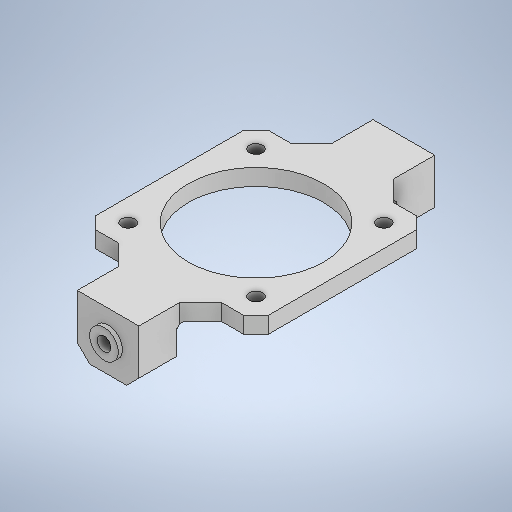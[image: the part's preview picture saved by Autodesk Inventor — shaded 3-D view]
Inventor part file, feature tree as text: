
AUTODESK INVENTOR PART (.ipt)
format: ipt  version: 2025 (Build 290162010, 162A)  size: 352,768 bytes
history: native  units: in
note: dims shown in document units (in); Inventor stores cm internally (conversion verified against a paired STEP export)
features: extrude x5, sketch x5, chamfer x3
ambient origin geometry x8: Origin, YZ Plane, XZ Plane, XY Plane, X Axis, Y Axis, Z Axis, Center Point
bodies: Body1 (feature_tree)
feature tree (13):
  extrude  "Extrusion24"  Depth=1.6535in
  extrude  "Extrusion25"  Depth=1.2248in
  extrude  "Extrusion26"  Depth=0.5906in
  chamfer  "Fasen5"  Distance=0.3642in
  chamfer  "Fasen6"  Distance=0.3642in
  chamfer  "Fasen7"  Distance=0.3937in
  extrude  "Extrusion29"  Depth=0.0394in
  extrude  "Extrusion30"  TaperAngle=0.0deg  [1 undecoded]
  sketch  "Skizze24"  dims[d120=1.6535in d121=1.2992in]
  sketch  "Skizze25"  dims[d122=0.128in d123=1.2248in]
  sketch  "Skizze26"  dims[d124=0.1575in d125=0.0in d126=0.5906in]
  sketch  "Skizze29"  dims[d127=0.5906in]
  sketch  "Skizze30"  dims[d128=0.5315in d129=0.3642in d130=0.3642in d131=0.3937in d132=0.0in d133=0.1319in d134=0.0in d135=0.0in d142=0.1181in d143=0.0787in d144=45.0deg d145=0.0492in d146=0.0787in d147=45.0deg d148=0.1969in d149=0.0787in d150=45.0deg d151=0.2756in d152=0.0394in d153=0.0in d154=0.2756in d155=0.0394in d156=0.0in d37=0.0197in d38=0.0344in d39=0.0197in d40=0.0344in d41=0.0197in d42=0.0344in]
note: 1 required parameter value undecoded (feature->parameter linkage not recoverable at this tier; creation-order binding heuristic only, values carry confidence <= 0.55)
